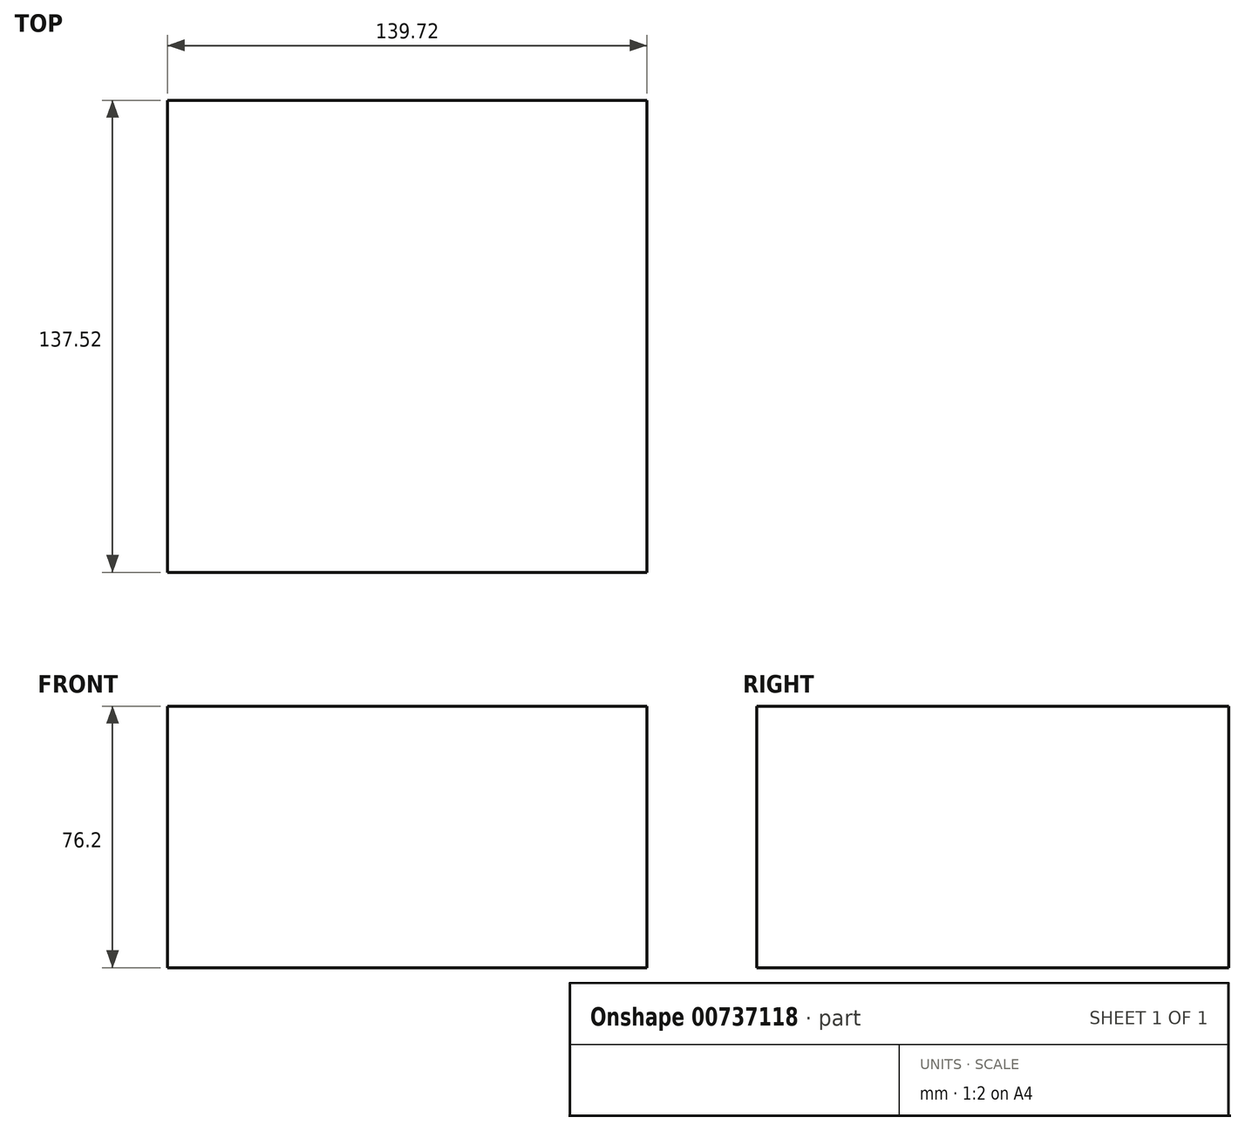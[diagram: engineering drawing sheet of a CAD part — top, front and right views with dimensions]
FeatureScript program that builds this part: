
annotation { "Feature Type Name" : "Feature", "Feature Type Description" : "" }
export const myFeature = defineFeature(function(context is Context, id is Id, definition is map)
    precondition{}
    {
        {
            var Q0;
            Q0=qCreatedBy(makeId("Top.planeOp"),FACE);
            var sketch = newSketch(context, id + "F0", { "sketchPlane" : qUnion([Q0])});
            skLineSegment(sketch, "E0.bottom", {"start": v(69.86, -68.76) * mm, "end": v(-69.86, -68.76) * mm});
            skLineSegment(sketch, "E0.top", {"start": v(69.86, 68.76) * mm, "end": v(-69.86, 68.76) * mm});
            skLineSegment(sketch, "E0.left", {"start": v(69.86, -68.76) * mm, "end": v(69.86, 68.76) * mm});
            skLineSegment(sketch, "E0.right", {"start": v(-69.86, -68.76) * mm, "end": v(-69.86, 68.76) * mm});
            skPoint(sketch, "E0.middle", {"position": v(0, 0) * mm});
            skLineSegment(sketch, "E1", {"start": v(0, 68.76) * mm, "end": v(0, -68.76) * mm});
            skSolve(sketch);
        }
        {
            var Q0;
            Q0=qCreatedBy(makeId("Top.planeOp"),FACE);
            var sketch = newSketch(context, id + "F1", { "sketchPlane" : qUnion([Q0])});
            skCircle(sketch, "E2", {"center": v(54.26, 0) * mm, "radius": 9.82 * mm});
            skSolve(sketch);
        }
        {
            var Q0;
            {var subQ0=sQuery(id+"F0.wireOp",EDGE,"E0.left");Q0=makeQuery(id+"F0.imprint","IMPRINT",FACE,{"disambiguationData":[TD([[makeQuery(id+"F0.imprint","IMPRINT",EDGE,{"derivedFrom":subQ0}),1.0]])]});}
            var Q1;
            {var subQ0=sQuery(id+"F0.wireOp",EDGE,"E0.right");Q1=makeQuery(id+"F0.imprint","IMPRINT",FACE,{"disambiguationData":[TD([[makeQuery(id+"F0.imprint","IMPRINT",EDGE,{"derivedFrom":subQ0}),-1.0]])]});}
            extrude(context, id + "F2", {"entities" : qUnion([Q0, Q1]), "depth" : 76.2 * mm, "offsetDistance" : 25.4 * mm});
        }
        {
            var Q0;
            Q0=sQuery(id+"F1.wireOp",EDGE,"E2");
            var Q1;
            Q1=sQuery(id+"F0.wireOp",EDGE,"E1");
            revolve(context, id + "F3", {"bodyType" : ToolBodyType.SURFACE, "surfaceOperationType" : NewSurfaceOperationType.NEW, "surfaceEntities" : qUnion([Q0]), "axis" : qUnion([Q1]), "revolveType" : RevolveType.FULL});
        }
    });
